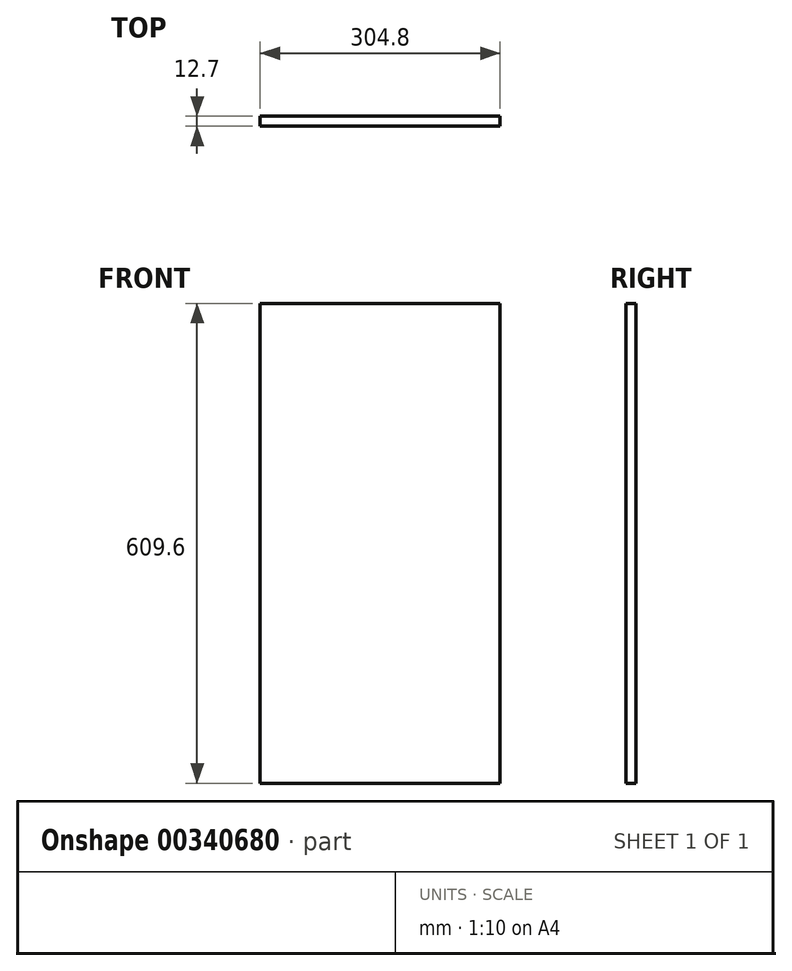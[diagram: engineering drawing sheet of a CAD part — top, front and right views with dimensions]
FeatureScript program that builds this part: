
annotation { "Feature Type Name" : "Feature", "Feature Type Description" : "" }
export const myFeature = defineFeature(function(context is Context, id is Id, definition is map)
    precondition{}
    {
        {
            var Q0;
            Q0=qCreatedBy(makeId("Front.planeOp"),FACE);
            var sketch = newSketch(context, id + "F0", { "sketchPlane" : qUnion([Q0])});
            skLineSegment(sketch, "E0.bottom", {"start": v(-155.1, 515.78) * mm, "end": v(149.7, 515.78) * mm});
            skLineSegment(sketch, "E0.top", {"start": v(-155.1, -93.82) * mm, "end": v(149.7, -93.82) * mm});
            skLineSegment(sketch, "E0.left", {"start": v(-155.1, 515.78) * mm, "end": v(-155.1, -93.82) * mm});
            skLineSegment(sketch, "E0.right", {"start": v(149.7, 515.78) * mm, "end": v(149.7, -93.82) * mm});
            skSolve(sketch);
        }
        {
            var Q0;
            Q0 = qSketchRegion(id + "F0", true);
            extrude(context, id + "F1", {"entities" : qUnion([Q0]), "depth" : 12.7 * mm});
        }
    });
